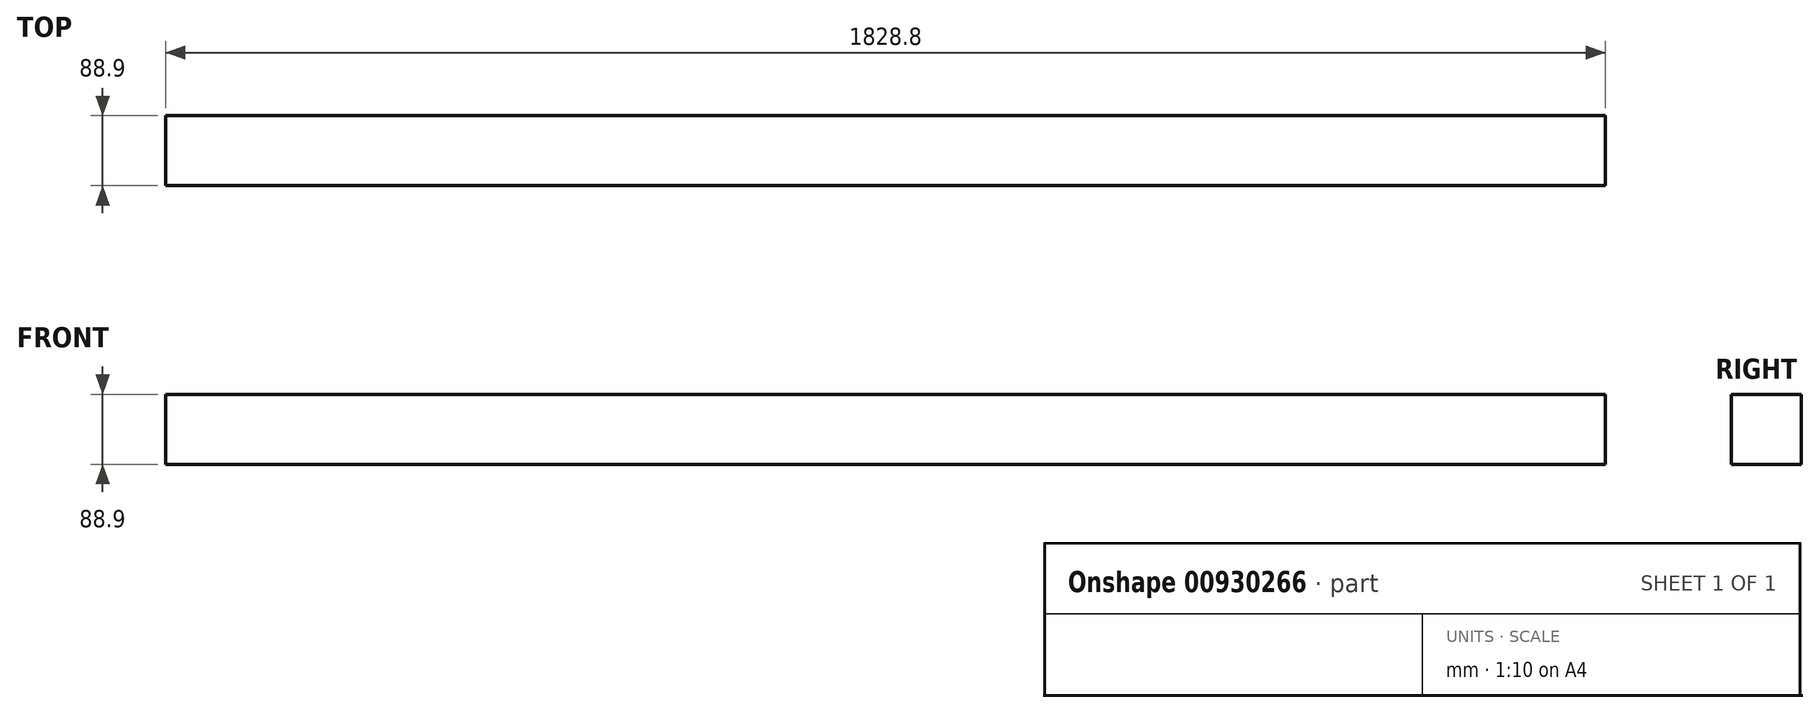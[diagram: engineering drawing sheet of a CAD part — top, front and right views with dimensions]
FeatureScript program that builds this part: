
annotation { "Feature Type Name" : "Feature", "Feature Type Description" : "" }
export const myFeature = defineFeature(function(context is Context, id is Id, definition is map)
    precondition{}
    {
        {
            var Q0;
            Q0=qCreatedBy(makeId("Right.planeOp"),FACE);
            var sketch = newSketch(context, id + "F0", { "sketchPlane" : qUnion([Q0])});
            skLineSegment(sketch, "E0.bottom", {"start": v(44.45, -44.45) * mm, "end": v(-44.45, -44.45) * mm});
            skLineSegment(sketch, "E0.top", {"start": v(44.45, 44.45) * mm, "end": v(-44.45, 44.45) * mm});
            skLineSegment(sketch, "E0.left", {"start": v(44.45, -44.45) * mm, "end": v(44.45, 44.45) * mm});
            skLineSegment(sketch, "E0.right", {"start": v(-44.45, -44.45) * mm, "end": v(-44.45, 44.45) * mm});
            skPoint(sketch, "E0.middle", {"position": v(0, 0) * mm});
            skSolve(sketch);
        }
        {
            var Q0;
            Q0=qSketchRegion(id+"F0",true);
            extrude(context, id + "F1", {"entities" : qUnion([Q0]), "endBound" : BoundingType.SYMMETRIC, "depth" : 1828.8 * mm});
        }
    });
